# Revit family: equip-faucet-elkay-lkd208513-l
name_source: partatom
category: Plumbing Fixtures
units: mm (PartAtom-declared; Revit-internal decimal feet)

## family parameters
Always vertical = Yes
Cut with Voids When Loaded = No
OmniClass Number = 23.45.55.17
OmniClass Title = Mixing Faucets
Part Type = Normal
Room Calculation Point = No
Round Connector Dimension = Use Radius
Shared = No
Work Plane-Based = Yes

## types (1)
- equip-faucet-elkay-lkd208513-l
    Assembly Code = D2010900
    CW Flow Rate = 2 GPM
    Cost = 0 $
    Default Elevation = 3' - 0"
    Faucet Material = Metal - Steel - Stainless - Chrome
    HW Flow Rate = 2 GPM
    Manufacturer = Elkay Manufacturing
    MasterFormat Number = 22 42 39
    MasterFormat Title = Commercial Faucets
    Nominal Dia = 0' - 0 3/8"
    Nominal Radius = 0' - 0 3/16"
    OmniClass Code = 23.45.55.17
    OmniClass Title = Mixing Faucets
    Specification URL = http://www.elkayusa.com
    Stem Material = Metal - Steel
    URL = www.elkayusa.com

## geometry (parser evidence)
native form markers: Sweep x3
no freeform markers — native parametric forms only
